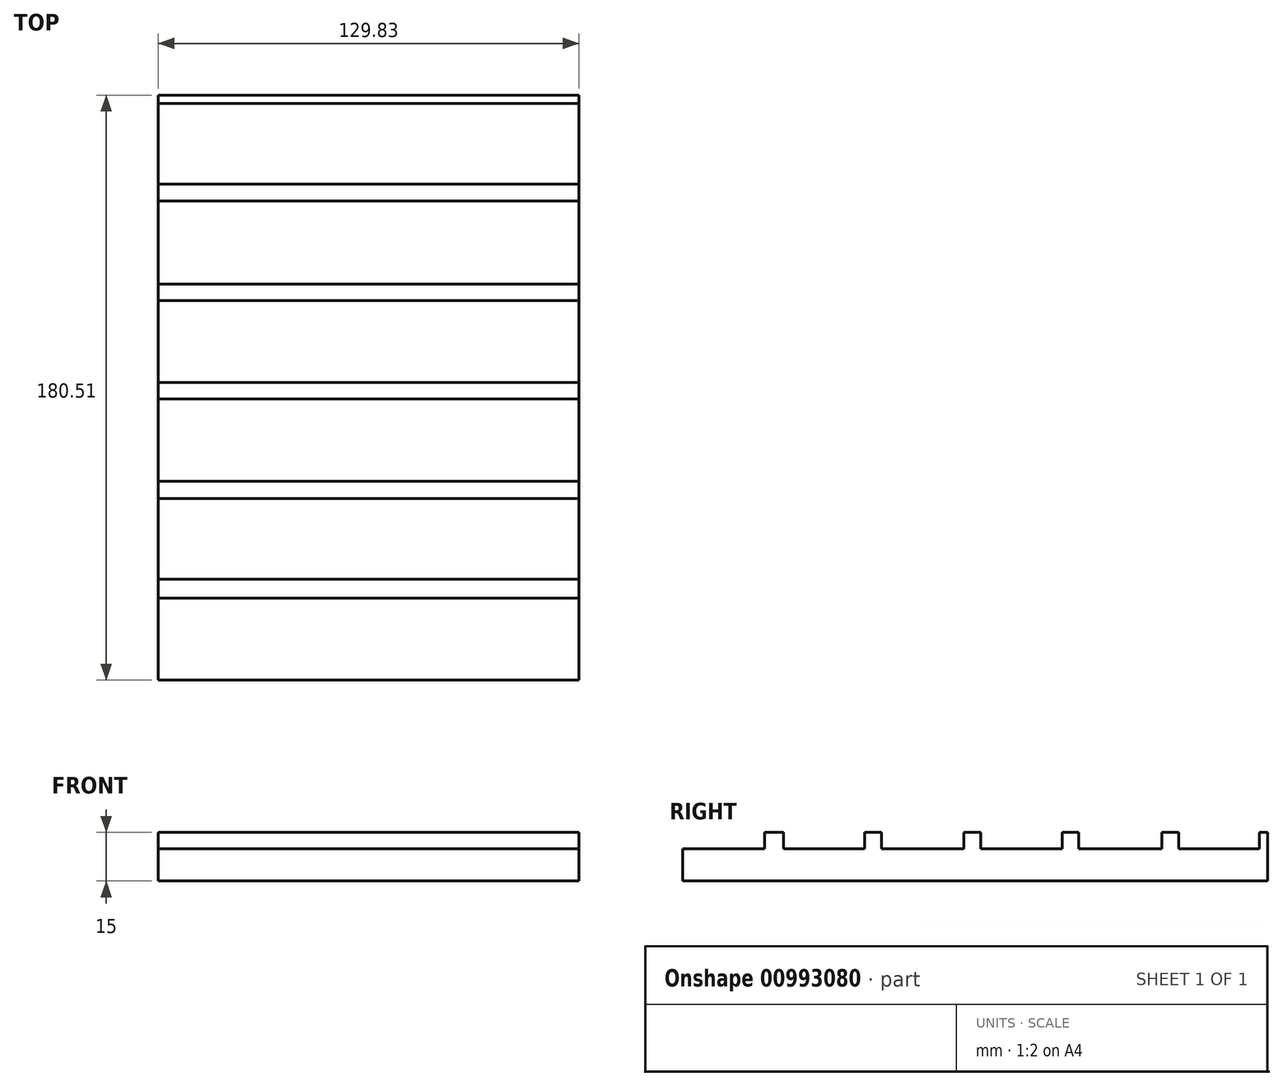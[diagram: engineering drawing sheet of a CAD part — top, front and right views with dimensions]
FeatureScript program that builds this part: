
annotation { "Feature Type Name" : "Feature", "Feature Type Description" : "" }
export const myFeature = defineFeature(function(context is Context, id is Id, definition is map)
    precondition{}
    {
        {
            var Q0;
            Q0=qCreatedBy(makeId("Top.planeOp"),FACE);
            var sketch = newSketch(context, id + "F0", { "sketchPlane" : qUnion([Q0])});
            skLineSegment(sketch, "E0.bottom", {"start": v(-69.9, -65.04) * mm, "end": v(59.93, -65.04) * mm});
            skLineSegment(sketch, "E0.top", {"start": v(-69.9, 115.47) * mm, "end": v(59.93, 115.47) * mm});
            skLineSegment(sketch, "E0.left", {"start": v(-69.9, -65.04) * mm, "end": v(-69.9, 115.47) * mm});
            skLineSegment(sketch, "E0.right", {"start": v(59.93, -65.04) * mm, "end": v(59.93, 115.47) * mm});
            skSolve(sketch);
        }
        {
            var Q0;
            Q0=makeQuery(id+"F0.imprint","IMPRINT",FACE,{"disambiguationData":[TD([[makeQuery(id+"F0.imprint","IMPRINT",EDGE,{"derivedFrom":sQuery(id+"F0.wireOp",EDGE,"E0.bottom")}),1.0]])]});
            extrude(context, id + "F1", {"entities" : qUnion([Q0]), "depth" : 15 * mm, "offsetDistance" : 25 * mm});
        }
        {
            var Q0;
            Q0=makeQuery(id+"F1.opExtrude","CAP_FACE",FACE,{"disambiguationData":[OSD([sQuery(id+"F0.wireOp",EDGE,"E0.bottom"),sQuery(id+"F0.wireOp",EDGE,"E0.top"),sQuery(id+"F0.wireOp",EDGE,"E0.left"),sQuery(id+"F0.wireOp",EDGE,"E0.right")])],"isStart":false});
            var sketch = newSketch(context, id + "F2", { "sketchPlane" : qUnion([Q0])});
            skLineSegment(sketch, "E1.bottom", {"start": v(-69.9, -65.04) * mm, "end": v(59.93, -65.04) * mm});
            skLineSegment(sketch, "E1.top", {"start": v(-69.9, -39.8) * mm, "end": v(59.93, -39.8) * mm});
            skLineSegment(sketch, "E1.left", {"start": v(-69.9, -65.04) * mm, "end": v(-69.9, -39.8) * mm});
            skLineSegment(sketch, "E1.right", {"start": v(59.93, -65.04) * mm, "end": v(59.93, -39.8) * mm});
            skSolve(sketch);
        }
        {
            var Q0;
            {var subQ0=sQuery(id+"F2.wireOp",EDGE,"E1.top");Q0=makeQuery(id+"F2.imprint","IMPRINT",FACE,{"disambiguationData":[TD([[makeQuery(id+"F2.imprint","IMPRINT",EDGE,{"derivedFrom":subQ0}),1.0]])]});}
            var sketch = newSketch(context, id + "F3", { "sketchPlane" : qUnion([Q0])});
            skLineSegment(sketch, "E2.bottom", {"start": v(-93.04, -33.86) * mm, "end": v(71.9, -33.86) * mm});
            skLineSegment(sketch, "E2.top", {"start": v(-93.04, -8.95) * mm, "end": v(71.9, -8.95) * mm});
            skLineSegment(sketch, "E2.left", {"start": v(-93.04, -33.86) * mm, "end": v(-93.04, -8.95) * mm});
            skLineSegment(sketch, "E2.right", {"start": v(71.9, -33.86) * mm, "end": v(71.9, -8.95) * mm});
            skSolve(sketch);
        }
        {
            var Q0;
            Q0=makeQuery(id+"F2.imprint","IMPRINT",FACE,{"disambiguationData":[TD([[makeQuery(id+"F2.imprint","IMPRINT",EDGE,{"derivedFrom":sQuery(id+"F2.wireOp",EDGE,"E1.bottom")}),1.0]])]});
            extrude(context, id + "F4", {"entities" : qUnion([Q0]), "operationType" : NewBodyOperationType.REMOVE, "oppositeDirection" : true, "depth" : 5 * mm, "offsetDistance" : 25 * mm});
        }
        {
            var Q0;
            Q0=makeQuery(id+"F3.imprint","IMPRINT",FACE,{"disambiguationData":[TD([[makeQuery(id+"F3.imprint","IMPRINT",EDGE,{"derivedFrom":sQuery(id+"F3.wireOp",EDGE,"E2.bottom")}),1.0]])]});
            extrude(context, id + "F5", {"entities" : qUnion([Q0]), "operationType" : NewBodyOperationType.REMOVE, "oppositeDirection" : true, "depth" : 5 * mm, "offsetDistance" : 25 * mm});
        }
        {
            var Q0;
            {var subQ0=sQuery(id+"F0.wireOp",EDGE,"E0.top");var subQ1=sQuery(id+"F0.wireOp",EDGE,"E0.left");var subQ2=sQuery(id+"F0.wireOp",EDGE,"E0.right");Q0=makeQuery(id+"F5.boolean.opBoolean","SPLIT",FACE,{"disambiguationData":[TD([makeQuery(id+"F1.opExtrude","SWEPT_FACE",FACE,{"disambiguationData":[OSD([subQ0])]})])],"derivedFrom":makeQuery(id+"F1.opExtrude","CAP_FACE",FACE,{"disambiguationData":[OSD([sQuery(id+"F0.wireOp",EDGE,"E0.bottom"),subQ0,subQ1,subQ2])],"isStart":false})});}
            var sketch = newSketch(context, id + "F6", { "sketchPlane" : qUnion([Q0])});
            skLineSegment(sketch, "E3.bottom", {"start": v(-69.9, -8.95) * mm, "end": v(59.93, -8.95) * mm});
            skLineSegment(sketch, "E3.top", {"start": v(-69.9, -3.9) * mm, "end": v(59.93, -3.9) * mm});
            skLineSegment(sketch, "E3.left", {"start": v(-69.9, -8.95) * mm, "end": v(-69.9, -3.9) * mm});
            skLineSegment(sketch, "E3.right", {"start": v(59.93, -8.95) * mm, "end": v(59.93, -3.9) * mm});
            skSolve(sketch);
        }
        {
            var Q0;
            {var subQ0=sQuery(id+"F6.wireOp",EDGE,"E3.top");Q0=makeQuery(id+"F6.imprint","IMPRINT",FACE,{"disambiguationData":[TD([[makeQuery(id+"F6.imprint","IMPRINT",EDGE,{"derivedFrom":subQ0}),1.0]])]});}
            var sketch = newSketch(context, id + "F7", { "sketchPlane" : qUnion([Q0])});
            skLineSegment(sketch, "E4.bottom", {"start": v(-86.4, -3.67) * mm, "end": v(107.52, -3.67) * mm});
            skLineSegment(sketch, "E4.top", {"start": v(-86.4, 21.77) * mm, "end": v(107.52, 21.77) * mm});
            skLineSegment(sketch, "E4.left", {"start": v(-86.4, -3.67) * mm, "end": v(-86.4, 21.77) * mm});
            skLineSegment(sketch, "E4.right", {"start": v(107.52, -3.67) * mm, "end": v(107.52, 21.77) * mm});
            skSolve(sketch);
        }
        {
            var Q0;
            Q0 = qSketchRegion(id + "F7", true);
            extrude(context, id + "F8", {"entities" : qUnion([Q0]), "operationType" : NewBodyOperationType.REMOVE, "oppositeDirection" : true, "depth" : 5 * mm, "offsetDistance" : 25 * mm});
        }
        {
            var Q0;
            {var subQ0=sQuery(id+"F0.wireOp",EDGE,"E0.top");var subQ1=makeQuery(id+"F1.opExtrude","SWEPT_FACE",FACE,{"disambiguationData":[OSD([subQ0])]});var subQ2=sQuery(id+"F0.wireOp",EDGE,"E0.left");var subQ4=sQuery(id+"F0.wireOp",EDGE,"E0.right");Q0=makeQuery(id+"F8.boolean.opBoolean","SPLIT",FACE,{"disambiguationData":[TD([subQ1])],"derivedFrom":makeQuery(id+"F5.boolean.opBoolean","SPLIT",FACE,{"disambiguationData":[TD([subQ1])],"derivedFrom":makeQuery(id+"F1.opExtrude","CAP_FACE",FACE,{"disambiguationData":[OSD([sQuery(id+"F0.wireOp",EDGE,"E0.bottom"),subQ0,subQ2,subQ4])],"isStart":false})})});}
            var sketch = newSketch(context, id + "F9", { "sketchPlane" : qUnion([Q0])});
            skLineSegment(sketch, "E5.bottom", {"start": v(-69.9, 21.77) * mm, "end": v(59.93, 21.77) * mm});
            skLineSegment(sketch, "E5.top", {"start": v(-69.9, 26.86) * mm, "end": v(59.93, 26.86) * mm});
            skLineSegment(sketch, "E5.left", {"start": v(-69.9, 21.77) * mm, "end": v(-69.9, 26.86) * mm});
            skLineSegment(sketch, "E5.right", {"start": v(59.93, 21.77) * mm, "end": v(59.93, 26.86) * mm});
            skLineSegment(sketch, "E6.top", {"start": v(-69.9, 52.07) * mm, "end": v(59.93, 52.07) * mm});
            skLineSegment(sketch, "E6.left", {"start": v(-69.9, 26.86) * mm, "end": v(-69.9, 52.07) * mm});
            skLineSegment(sketch, "E6.right", {"start": v(59.93, 26.86) * mm, "end": v(59.93, 52.07) * mm});
            skLineSegment(sketch, "E7.top", {"start": v(-69.9, 57.2) * mm, "end": v(59.93, 57.2) * mm});
            skLineSegment(sketch, "E7.left", {"start": v(-69.9, 52.07) * mm, "end": v(-69.9, 57.2) * mm});
            skLineSegment(sketch, "E7.right", {"start": v(59.93, 52.07) * mm, "end": v(59.93, 57.2) * mm});
            skLineSegment(sketch, "E8.top", {"start": v(-69.9, 82.84) * mm, "end": v(59.93, 82.84) * mm});
            skLineSegment(sketch, "E8.left", {"start": v(-69.9, 57.2) * mm, "end": v(-69.9, 82.84) * mm});
            skLineSegment(sketch, "E8.right", {"start": v(59.93, 57.2) * mm, "end": v(59.93, 82.84) * mm});
            skLineSegment(sketch, "E9.top", {"start": v(-69.9, 87.97) * mm, "end": v(59.93, 87.97) * mm});
            skLineSegment(sketch, "E9.left", {"start": v(-69.9, 82.84) * mm, "end": v(-69.9, 87.97) * mm});
            skLineSegment(sketch, "E9.right", {"start": v(59.93, 82.84) * mm, "end": v(59.93, 87.97) * mm});
            skLineSegment(sketch, "E10.top", {"start": v(-69.9, 112.91) * mm, "end": v(59.93, 112.91) * mm});
            skLineSegment(sketch, "E10.left", {"start": v(-69.9, 87.97) * mm, "end": v(-69.9, 112.91) * mm});
            skLineSegment(sketch, "E10.right", {"start": v(59.93, 87.97) * mm, "end": v(59.93, 112.91) * mm});
            skSolve(sketch);
        }
        {
            var Q0;
            Q0=makeQuery(id+"F9.imprint","IMPRINT",FACE,{"disambiguationData":[TD([[makeQuery(id+"F9.imprint","IMPRINT",EDGE,{"derivedFrom":sQuery(id+"F9.wireOp",EDGE,"E9.top")}),1.0]])]});
            var Q1;
            Q1=makeQuery(id+"F9.imprint","IMPRINT",FACE,{"disambiguationData":[TD([[makeQuery(id+"F9.imprint","IMPRINT",EDGE,{"derivedFrom":sQuery(id+"F9.wireOp",EDGE,"E7.top")}),1.0]])]});
            var Q2;
            Q2=makeQuery(id+"F9.imprint","IMPRINT",FACE,{"disambiguationData":[TD([[makeQuery(id+"F9.imprint","IMPRINT",EDGE,{"derivedFrom":sQuery(id+"F9.wireOp",EDGE,"E5.top")}),1.0]])]});
            extrude(context, id + "F10", {"entities" : qUnion([Q0, Q1, Q2]), "operationType" : NewBodyOperationType.REMOVE, "oppositeDirection" : true, "depth" : 5 * mm, "offsetDistance" : 25 * mm});
        }
    });
